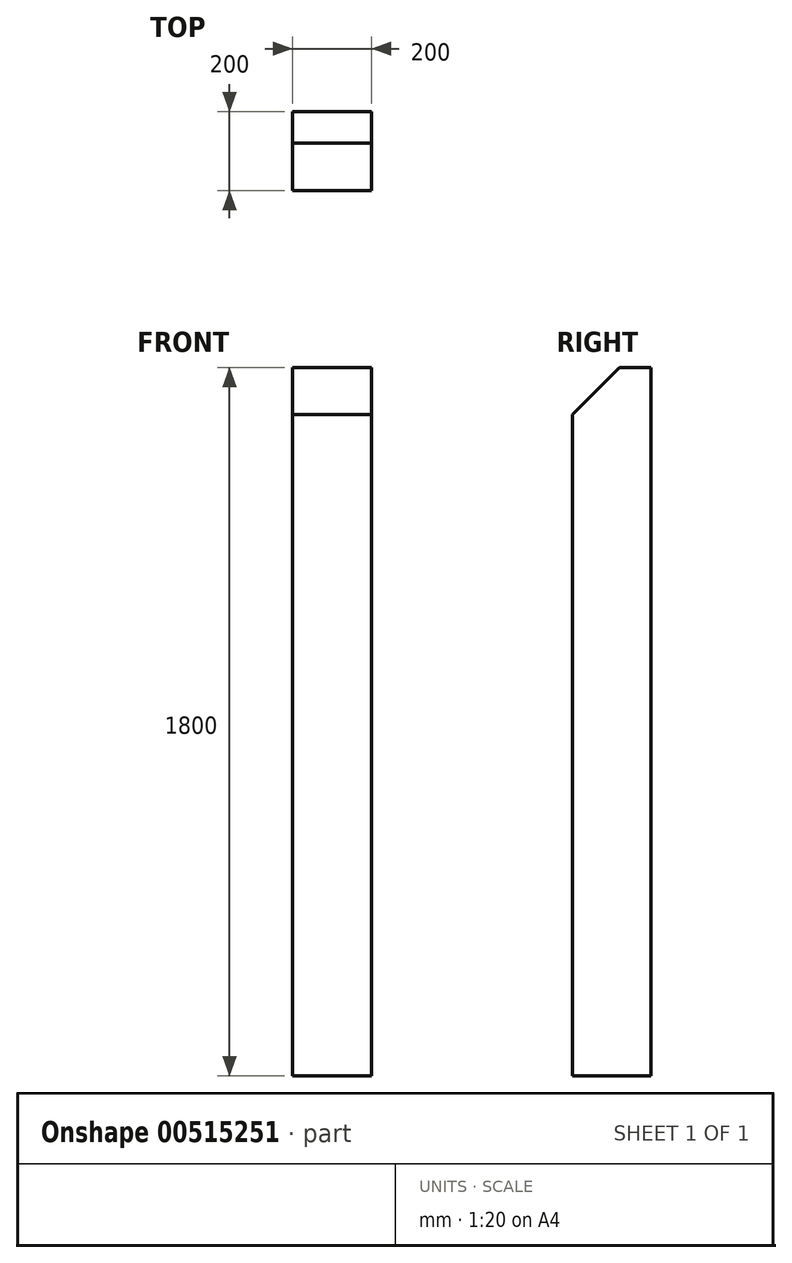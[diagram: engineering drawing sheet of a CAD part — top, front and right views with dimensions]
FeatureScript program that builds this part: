
annotation { "Feature Type Name" : "Feature", "Feature Type Description" : "" }
export const myFeature = defineFeature(function(context is Context, id is Id, definition is map)
    precondition{}
    {
        {
            var Q0;
            Q0=qCreatedBy(makeId("Top.planeOp"),FACE);
            var sketch = newSketch(context, id + "F0", { "sketchPlane" : qUnion([Q0])});
            skLineSegment(sketch, "E0.bottom", {"start": v(100, -100) * mm, "end": v(-100, -100) * mm});
            skLineSegment(sketch, "E0.top", {"start": v(100, 100) * mm, "end": v(-100, 100) * mm});
            skLineSegment(sketch, "E0.left", {"start": v(100, -100) * mm, "end": v(100, 100) * mm});
            skLineSegment(sketch, "E0.right", {"start": v(-100, -100) * mm, "end": v(-100, 100) * mm});
            skPoint(sketch, "E0.middle", {"position": v(0, 0) * mm});
            skSolve(sketch);
        }
        {
            var Q0;
            Q0=makeQuery(id+"F0.imprint","IMPRINT",FACE,{"disambiguationData":[TD([[makeQuery(id+"F0.imprint","IMPRINT",EDGE,{"derivedFrom":sQuery(id+"F0.wireOp",EDGE,"E0.bottom")}),-1.0]])]});
            extrude(context, id + "F1", {"entities" : qUnion([Q0]), "depth" : 1000 * mm, "offsetDistance" : 25 * mm, "hasSecondDirection" : true, "secondDirectionOppositeDirection" : true, "secondDirectionDepth" : 800 * mm});
        }
        {
            var Q0;
            Q0=makeQuery(id+"F1.opExtrude","CAP_EDGE",EDGE,{"disambiguationData":[OSD([sQuery(id+"F0.wireOp",EDGE,"E0.bottom")])],"isStart":false});
            chamfer(context, id + "F2", {"entities" : qUnion([Q0]), "width" : 120 * mm, "tangentPropagation" : true});
        }
    });
